# Revit family: CADS_Vent-Axia_MechEquip_Fan_EMF_3Ph4P - SUPPLY
name_source: partatom
category: Mechanical Equipment
units: mm (PartAtom-declared; Revit-internal decimal feet)

## family parameters
Always vertical = Yes
Cut with Voids When Loaded = No
OmniClass Number = 23.75.00.00
OmniClass Title = Climate Control (HVAC)
Part Type = Normal
Room Calculation Point = No
Round Connector Dimension = Use Diameter
Shared = No
Work Plane-Based = No

## types (6) — shared parameters
AirflowRateRange = 0.0 L/s
AssemblyPlace = UNKNOWN
AssetType = FIXED
DurationUnit = Year
ExteriorInsulation = No
Fitting Type = Ignore
GrossWeight = 0.00 kg
HasProtectiveEarth = No
IfcExportAs = IfcFanType
IsExtendedWarranty = No
ManufacturerAddress = Fleming Way
Crawley 
RH10 9YX
Quantity = 1
RatedCurrent = 0 A
RatedVoltage = 0 V
Status = New
WarrantyGuarantor = Vent-Axia Limited
WorkingPressure = 0.0 Pa
zero-valued in all types: CADS_Index, CADS_Usage, Default Elevation, ExpectedServiceLife, NumberOfPoles

## per-type parameters (varying)
| type | ModelReference | NominalDiameter | NominalHeight | NominalLength | NominalWidth |
| EMF40034 | 400mm ECO MIXED FLOW FAN 3 PHASE 4 POLE | 400 mm  [stored 1.31234 ft] | 400 mm  [stored 1.31234 ft] | 515 mm  [stored 1.68963 ft] | 400 mm  [stored 1.31234 ft] |
| EMF45034 | 450mm ECO MIXED FLOW FAN 3 PHASE 4 POLE | 450 mm  [stored 1.47638 ft] | 450 mm  [stored 1.47638 ft] | 467 mm  [stored 1.53215 ft] | 450 mm  [stored 1.47638 ft] |
| EMF50034 | 500mm ECO MIXED FLOW FAN 3 PHASE 4 POLE | 500 mm  [stored 1.64042 ft] | 500 mm  [stored 1.64042 ft] | 515 mm  [stored 1.68963 ft] | 500 mm  [stored 1.64042 ft] |
| EMF56034 | 560mm ECO MIXED FLOW FAN 3 PHASE 4 POLE | 560 mm  [stored 1.83727 ft] | 560 mm  [stored 1.83727 ft] | 582 mm  [stored 1.90945 ft] | 560 mm  [stored 1.83727 ft] |
| EMF63034 | 630mm ECO MIXED FLOW FAN 3 PHASE 4 POLE | 630 mm  [stored 2.06693 ft] | 630 mm  [stored 2.06693 ft] | 654 mm | 630 mm  [stored 2.06693 ft] |
| EMF71034 | 710mm ECO MIXED FLOW FAN 3 PHASE 4 POLE | 710 mm | 710 mm | 732 mm | 710 mm |

note: column(s) folded — value = type name in every type: ModelNumber

note: [stored X ft] marks values corroborated as IEEE doubles in the binary element streams (Revit-internal decimal feet)

## geometry (parser evidence)
native form markers: Sweep x12
no freeform markers — native parametric forms only
